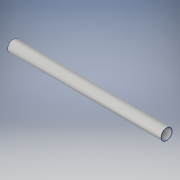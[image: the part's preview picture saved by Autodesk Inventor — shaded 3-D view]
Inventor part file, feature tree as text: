
AUTODESK INVENTOR PART (.ipt)
format: ipt  version: 2017 SP1 (Build 210196100, 196)  size: 95,744 bytes
history: native  units: in
note: dims shown in document units (in); Inventor stores cm internally (conversion verified against a paired STEP export)
features: extrude x1, sketch x1
ambient origin geometry x8: Origin, YZ Plane, XZ Plane, XY Plane, X Axis, Y Axis, Z Axis, Center Point
bodies: Solid1 (feature_tree)
feature tree (2):
  extrude  "Extrusion1"  Depth=108.0in
  sketch  "Sketch1"  dims[d0=7.5in d1=8.0in d2=108.0in d3=0.0in]
